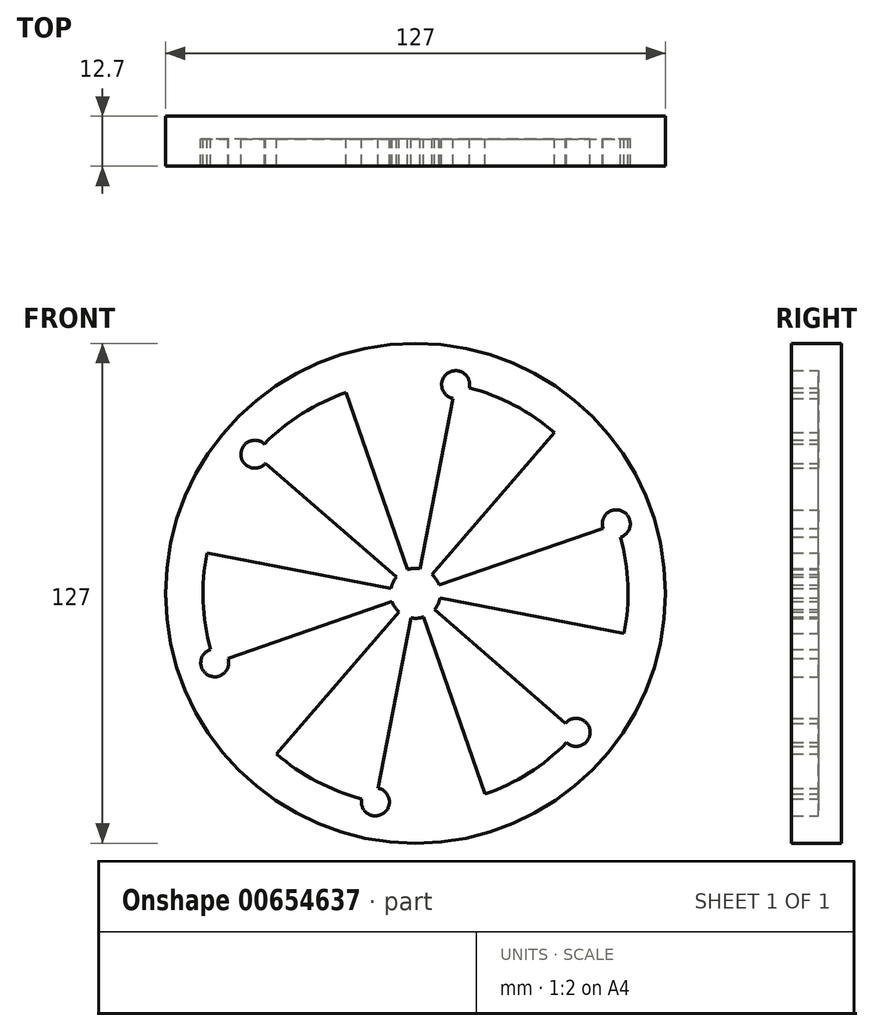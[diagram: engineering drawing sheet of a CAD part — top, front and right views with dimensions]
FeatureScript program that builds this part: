
annotation { "Feature Type Name" : "Feature", "Feature Type Description" : "" }
export const myFeature = defineFeature(function(context is Context, id is Id, definition is map)
    precondition{}
    {
        {
            var Q0;
            Q0=qCreatedBy(makeId("Front.planeOp"),FACE);
            var sketch = newSketch(context, id + "F0", { "sketchPlane" : qUnion([Q0])});
            skCircle(sketch, "E0", {"center": v(0, 0) * mm, "radius": 63.5 * mm});
            skLineSegment(sketch, "E1", {"start": v(0, 0) * mm, "end": v(48, -41.57) * mm});
            skLineSegment(sketch, "E2", {"start": v(0, 0) * mm, "end": v(41.57, 48) * mm});
            skLineSegment(sketch, "E3", {"start": v(0, 0) * mm, "end": v(-48, 41.57) * mm});
            skLineSegment(sketch, "E4", {"start": v(0, 0) * mm, "end": v(-41.57, -48) * mm});
            skLineSegment(sketch, "E5", {"start": v(0, 0) * mm, "end": v(20.79, -60) * mm});
            skLineSegment(sketch, "E6", {"start": v(0, 0) * mm, "end": v(-12, -62.36) * mm});
            skLineSegment(sketch, "E7", {"start": v(0, 0) * mm, "end": v(12, 62.36) * mm});
            skLineSegment(sketch, "E8", {"start": v(0, 0) * mm, "end": v(-20.79, 60) * mm});
            skLineSegment(sketch, "E9", {"start": v(0, 0) * mm, "end": v(62.36, -12) * mm});
            skLineSegment(sketch, "E10", {"start": v(0, 0) * mm, "end": v(60, 20.79) * mm});
            skPoint(sketch, "E10.endSnap0", {"position": v(-24, 20.79) * mm});
            skLineSegment(sketch, "E11", {"start": v(0, 0) * mm, "end": v(-60, -20.79) * mm});
            skLineSegment(sketch, "E12", {"start": v(0, 0) * mm, "end": v(-62.36, 12) * mm});
            skCircle(sketch, "E13", {"center": v(0, 0) * mm, "radius": 53.98 * mm});
            skCircle(sketch, "E14", {"center": v(-40.8, 35.33) * mm, "radius": 3.56 * mm});
            skCircle(sketch, "E15", {"center": v(10.2, 53) * mm, "radius": 3.56 * mm});
            skCircle(sketch, "E16", {"center": v(51, 17.67) * mm, "radius": 3.56 * mm});
            skCircle(sketch, "E17", {"center": v(40.8, -35.33) * mm, "radius": 3.56 * mm});
            skCircle(sketch, "E18", {"center": v(-10.2, -53) * mm, "radius": 3.56 * mm});
            skCircle(sketch, "E19", {"center": v(-51, -17.67) * mm, "radius": 3.56 * mm});
            skCircle(sketch, "E20", {"center": v(0, 0) * mm, "radius": 6.35 * mm});
            skSolve(sketch);
        }
        {
            var Q0;
            {var subQ6=sQuery(id+"F0.wireOp",EDGE,"E0");var subQ9=sQuery(id+"F0.wireOp",EDGE,"E2");var subQ10=makeQuery(id+"F0.imprint","INTERSECT",VERTEX,{"derivedFrom":[subQ6,subQ9]});Q0=makeQuery(id+"F0.imprint","IMPRINT",FACE,{"disambiguationData":[TD([[makeQuery(id+"F0.imprint","IMPRINT",EDGE,{"disambiguationData":[TD([[subQ10,1.0]])],"derivedFrom":subQ6}),1.0]])]});}
            var Q1;
            {var subQ6=sQuery(id+"F0.wireOp",EDGE,"E0");var subQ9=sQuery(id+"F0.wireOp",EDGE,"E2");var subQ10=makeQuery(id+"F0.imprint","INTERSECT",VERTEX,{"derivedFrom":[subQ6,subQ9]});Q1=makeQuery(id+"F0.imprint","IMPRINT",FACE,{"disambiguationData":[TD([[makeQuery(id+"F0.imprint","IMPRINT",EDGE,{"disambiguationData":[TD([[subQ10,-1.0]])],"derivedFrom":subQ6}),1.0]])]});}
            var Q2;
            {var subQ5=sQuery(id+"F0.wireOp",EDGE,"E7");var subQ6=sQuery(id+"F0.wireOp",EDGE,"E0");var subQ7=makeQuery(id+"F0.imprint","INTERSECT",VERTEX,{"derivedFrom":[subQ6,subQ5]});Q2=makeQuery(id+"F0.imprint","IMPRINT",FACE,{"disambiguationData":[TD([[makeQuery(id+"F0.imprint","IMPRINT",EDGE,{"disambiguationData":[TD([[subQ7,-1.0]])],"derivedFrom":subQ6}),1.0]])]});}
            var Q3;
            {var subQ6=sQuery(id+"F0.wireOp",EDGE,"E0");var subQ9=sQuery(id+"F0.wireOp",EDGE,"E3");var subQ10=makeQuery(id+"F0.imprint","INTERSECT",VERTEX,{"derivedFrom":[subQ6,subQ9]});Q3=makeQuery(id+"F0.imprint","IMPRINT",FACE,{"disambiguationData":[TD([[makeQuery(id+"F0.imprint","IMPRINT",EDGE,{"disambiguationData":[TD([[subQ10,1.0]])],"derivedFrom":subQ6}),1.0]])]});}
            var Q4;
            {var subQ0=sQuery(id+"F0.wireOp",EDGE,"E3");var subQ1=sQuery(id+"F0.wireOp",EDGE,"E0");var subQ2=makeQuery(id+"F0.imprint","INTERSECT",VERTEX,{"derivedFrom":[subQ1,subQ0]});Q4=makeQuery(id+"F0.imprint","IMPRINT",FACE,{"disambiguationData":[TD([[makeQuery(id+"F0.imprint","IMPRINT",EDGE,{"disambiguationData":[TD([[subQ2,-1.0]])],"derivedFrom":subQ1}),1.0]])]});}
            var Q5;
            {var subQ5=sQuery(id+"F0.wireOp",EDGE,"E11");var subQ6=sQuery(id+"F0.wireOp",EDGE,"E0");var subQ7=makeQuery(id+"F0.imprint","INTERSECT",VERTEX,{"derivedFrom":[subQ6,subQ5]});Q5=makeQuery(id+"F0.imprint","IMPRINT",FACE,{"disambiguationData":[TD([[makeQuery(id+"F0.imprint","IMPRINT",EDGE,{"disambiguationData":[TD([[subQ7,1.0]])],"derivedFrom":subQ6}),1.0]])]});}
            var Q6;
            {var subQ6=sQuery(id+"F0.wireOp",EDGE,"E0");var subQ9=sQuery(id+"F0.wireOp",EDGE,"E4");var subQ10=makeQuery(id+"F0.imprint","INTERSECT",VERTEX,{"derivedFrom":[subQ6,subQ9]});Q6=makeQuery(id+"F0.imprint","IMPRINT",FACE,{"disambiguationData":[TD([[makeQuery(id+"F0.imprint","IMPRINT",EDGE,{"disambiguationData":[TD([[subQ10,1.0]])],"derivedFrom":subQ6}),1.0]])]});}
            var Q7;
            {var subQ6=sQuery(id+"F0.wireOp",EDGE,"E0");var subQ9=sQuery(id+"F0.wireOp",EDGE,"E4");var subQ11=makeQuery(id+"F0.imprint","INTERSECT",VERTEX,{"derivedFrom":[subQ6,subQ9]});Q7=makeQuery(id+"F0.imprint","IMPRINT",FACE,{"disambiguationData":[TD([[makeQuery(id+"F0.imprint","IMPRINT",EDGE,{"disambiguationData":[TD([[subQ11,-1.0]])],"derivedFrom":subQ6}),1.0]])]});}
            var Q8;
            {var subQ1=sQuery(id+"F0.wireOp",EDGE,"E0");var subQ9=sQuery(id+"F0.wireOp",EDGE,"E5");var subQ10=makeQuery(id+"F0.imprint","INTERSECT",VERTEX,{"derivedFrom":[subQ1,subQ9]});Q8=makeQuery(id+"F0.imprint","IMPRINT",FACE,{"disambiguationData":[TD([[makeQuery(id+"F0.imprint","IMPRINT",EDGE,{"disambiguationData":[TD([[subQ10,1.0]])],"derivedFrom":subQ1}),1.0]])]});}
            var Q9;
            {var subQ1=sQuery(id+"F0.wireOp",EDGE,"E0");var subQ5=sQuery(id+"F0.wireOp",EDGE,"E1");var subQ6=makeQuery(id+"F0.imprint","INTERSECT",VERTEX,{"derivedFrom":[subQ1,subQ5]});Q9=makeQuery(id+"F0.imprint","IMPRINT",FACE,{"disambiguationData":[TD([[makeQuery(id+"F0.imprint","IMPRINT",EDGE,{"disambiguationData":[TD([[subQ6,1.0]])],"derivedFrom":subQ1}),1.0]])]});}
            var Q10;
            {var subQ5=sQuery(id+"F0.wireOp",EDGE,"E1");var subQ6=sQuery(id+"F0.wireOp",EDGE,"E0");var subQ7=makeQuery(id+"F0.imprint","INTERSECT",VERTEX,{"derivedFrom":[subQ6,subQ5]});Q10=makeQuery(id+"F0.imprint","IMPRINT",FACE,{"disambiguationData":[TD([[makeQuery(id+"F0.imprint","IMPRINT",EDGE,{"disambiguationData":[TD([[subQ7,-1.0]])],"derivedFrom":subQ6}),1.0]])]});}
            var Q11;
            {var subQ6=sQuery(id+"F0.wireOp",EDGE,"E0");var subQ9=sQuery(id+"F0.wireOp",EDGE,"E9");var subQ10=makeQuery(id+"F0.imprint","INTERSECT",VERTEX,{"derivedFrom":[subQ6,subQ9]});Q11=makeQuery(id+"F0.imprint","IMPRINT",FACE,{"disambiguationData":[TD([[makeQuery(id+"F0.imprint","IMPRINT",EDGE,{"disambiguationData":[TD([[subQ10,-1.0]])],"derivedFrom":subQ6}),1.0]])]});}
            var Q12;
            {var subQ3=sQuery(id+"F0.wireOp",EDGE,"E13");var subQ7=sQuery(id+"F0.wireOp",EDGE,"bFVIDeSC-H81D-zjeg-pnwl-N6VgIu66khsg");var subQ9=makeQuery(id+"F0.imprint","INTERSECT",VERTEX,{"disambiguationData":[OD(1.0)],"derivedFrom":[subQ3,subQ7]});Q12=makeQuery(id+"F0.imprint","IMPRINT",FACE,{"disambiguationData":[TD([[makeQuery(id+"F0.imprint","IMPRINT",EDGE,{"disambiguationData":[TD([[subQ9,-1.0]])],"derivedFrom":subQ3}),1.0]])]});}
            var Q13;
            {var subQ0=sQuery(id+"F0.wireOp",EDGE,"E14");var subQ3=sQuery(id+"F0.wireOp",EDGE,"E13");var subQ4=makeQuery(id+"F0.imprint","INTERSECT",VERTEX,{"disambiguationData":[OD(1.0)],"derivedFrom":[subQ3,subQ0]});Q13=makeQuery(id+"F0.imprint","IMPRINT",FACE,{"disambiguationData":[TD([[makeQuery(id+"F0.imprint","IMPRINT",EDGE,{"disambiguationData":[TD([[subQ4,-1.0]])],"derivedFrom":subQ3}),1.0]])]});}
            var Q14;
            {var subQ3=sQuery(id+"F0.wireOp",EDGE,"E13");var subQ5=sQuery(id+"F0.wireOp",EDGE,"E18");var subQ6=makeQuery(id+"F0.imprint","INTERSECT",VERTEX,{"disambiguationData":[OD(1.0)],"derivedFrom":[subQ3,subQ5]});Q14=makeQuery(id+"F0.imprint","IMPRINT",FACE,{"disambiguationData":[TD([[makeQuery(id+"F0.imprint","IMPRINT",EDGE,{"disambiguationData":[TD([[subQ6,-1.0]])],"derivedFrom":subQ3}),1.0]])]});}
            var Q15;
            {var subQ3=sQuery(id+"F0.wireOp",EDGE,"E13");var subQ5=sQuery(id+"F0.wireOp",EDGE,"qDP75IfH-e56L-sAAi-RVnk-waoNLLPqcEhU");var subQ6=makeQuery(id+"F0.imprint","INTERSECT",VERTEX,{"disambiguationData":[OD(1.0)],"derivedFrom":[subQ3,subQ5]});Q15=makeQuery(id+"F0.imprint","IMPRINT",FACE,{"disambiguationData":[TD([[makeQuery(id+"F0.imprint","IMPRINT",EDGE,{"disambiguationData":[TD([[subQ6,-1.0]])],"derivedFrom":subQ3}),1.0]])]});}
            var Q16;
            {var subQ3=sQuery(id+"F0.wireOp",EDGE,"E13");var subQ5=sQuery(id+"F0.wireOp",EDGE,"KR1A6qMm-7GyC-ORdT-OOG4-rRh3sLOKavEw");var subQ6=makeQuery(id+"F0.imprint","INTERSECT",VERTEX,{"disambiguationData":[OD(1.0)],"derivedFrom":[subQ3,subQ5]});Q16=makeQuery(id+"F0.imprint","IMPRINT",FACE,{"disambiguationData":[TD([[makeQuery(id+"F0.imprint","IMPRINT",EDGE,{"disambiguationData":[TD([[subQ6,-1.0]])],"derivedFrom":subQ3}),1.0]])]});}
            var Q17;
            {var subQ0=sQuery(id+"F0.wireOp",EDGE,"E19");var subQ1=sQuery(id+"F0.wireOp",EDGE,"E13");var subQ2=makeQuery(id+"F0.imprint","INTERSECT",VERTEX,{"disambiguationData":[OD(1.0)],"derivedFrom":[subQ1,subQ0]});Q17=makeQuery(id+"F0.imprint","IMPRINT",FACE,{"disambiguationData":[TD([[makeQuery(id+"F0.imprint","IMPRINT",EDGE,{"disambiguationData":[TD([[subQ2,-1.0]])],"derivedFrom":subQ1}),1.0]])]});}
            var Q18;
            {var subQ3=sQuery(id+"F0.wireOp",EDGE,"E13");var subQ5=sQuery(id+"F0.wireOp",EDGE,"N1TDYXci-TAxV-rjYT-g8DT-FGwgl61c5ldQ");var subQ6=makeQuery(id+"F0.imprint","INTERSECT",VERTEX,{"disambiguationData":[OD(1.0)],"derivedFrom":[subQ3,subQ5]});Q18=makeQuery(id+"F0.imprint","IMPRINT",FACE,{"disambiguationData":[TD([[makeQuery(id+"F0.imprint","IMPRINT",EDGE,{"disambiguationData":[TD([[subQ6,-1.0]])],"derivedFrom":subQ3}),1.0]])]});}
            var Q19;
            {var subQ3=sQuery(id+"F0.wireOp",EDGE,"E13");var subQ5=sQuery(id+"F0.wireOp",EDGE,"E15");var subQ6=makeQuery(id+"F0.imprint","INTERSECT",VERTEX,{"disambiguationData":[OD(1.0)],"derivedFrom":[subQ3,subQ5]});Q19=makeQuery(id+"F0.imprint","IMPRINT",FACE,{"disambiguationData":[TD([[makeQuery(id+"F0.imprint","IMPRINT",EDGE,{"disambiguationData":[TD([[subQ6,-1.0]])],"derivedFrom":subQ3}),1.0]])]});}
            var Q20;
            {var subQ5=sQuery(id+"F0.wireOp",EDGE,"E13");var subQ7=sQuery(id+"F0.wireOp",EDGE,"E17");var subQ8=makeQuery(id+"F0.imprint","INTERSECT",VERTEX,{"disambiguationData":[OD(1.0)],"derivedFrom":[subQ5,subQ7]});Q20=makeQuery(id+"F0.imprint","IMPRINT",FACE,{"disambiguationData":[TD([[makeQuery(id+"F0.imprint","IMPRINT",EDGE,{"disambiguationData":[TD([[subQ8,-1.0]])],"derivedFrom":subQ5}),1.0]])]});}
            var Q21;
            {var subQ0=sQuery(id+"F0.wireOp",EDGE,"tmVU6iB4-Arpo-FPyW-8SLi-fDhzcNPMV2CL");var subQ1=sQuery(id+"F0.wireOp",EDGE,"E13");var subQ2=makeQuery(id+"F0.imprint","INTERSECT",VERTEX,{"disambiguationData":[OD(1.0)],"derivedFrom":[subQ1,subQ0]});Q21=makeQuery(id+"F0.imprint","IMPRINT",FACE,{"disambiguationData":[TD([[makeQuery(id+"F0.imprint","IMPRINT",EDGE,{"disambiguationData":[TD([[subQ2,-1.0]])],"derivedFrom":subQ1}),1.0]])]});}
            var Q22;
            {var subQ3=sQuery(id+"F0.wireOp",EDGE,"E13");var subQ5=sQuery(id+"F0.wireOp",EDGE,"E16");var subQ6=makeQuery(id+"F0.imprint","INTERSECT",VERTEX,{"disambiguationData":[OD(1.0)],"derivedFrom":[subQ3,subQ5]});Q22=makeQuery(id+"F0.imprint","IMPRINT",FACE,{"disambiguationData":[TD([[makeQuery(id+"F0.imprint","IMPRINT",EDGE,{"disambiguationData":[TD([[subQ6,-1.0]])],"derivedFrom":subQ3}),1.0]])]});}
            extrude(context, id + "F1", {"entities" : qUnion([Q0, Q1, Q2, Q3, Q4, Q5, Q6, Q7, Q8, Q9, Q10, Q11, Q12, Q13, Q14, Q15, Q16, Q17, Q18, Q19, Q20, Q21, Q22]), "depth" : 12.7 * mm, "offsetDistance" : 25.4 * mm});
        }
        {
            var Q0;
            Q0=qCreatedBy(makeId("Front.planeOp"),FACE);
            var sketch = newSketch(context, id + "F2", { "sketchPlane" : qUnion([Q0])});
            skCircle(sketch, "E21", {"center": v(0, 0) * mm, "radius": 63.5 * mm});
            skSolve(sketch);
        }
        {
            var Q0;
            Q0 = qSketchRegion(id + "F2", true);
            extrude(context, id + "F3", {"entities" : qUnion([Q0]), "operationType" : NewBodyOperationType.ADD, "depth" : 5.84 * mm, "offsetDistance" : 25.4 * mm});
        }
    });
